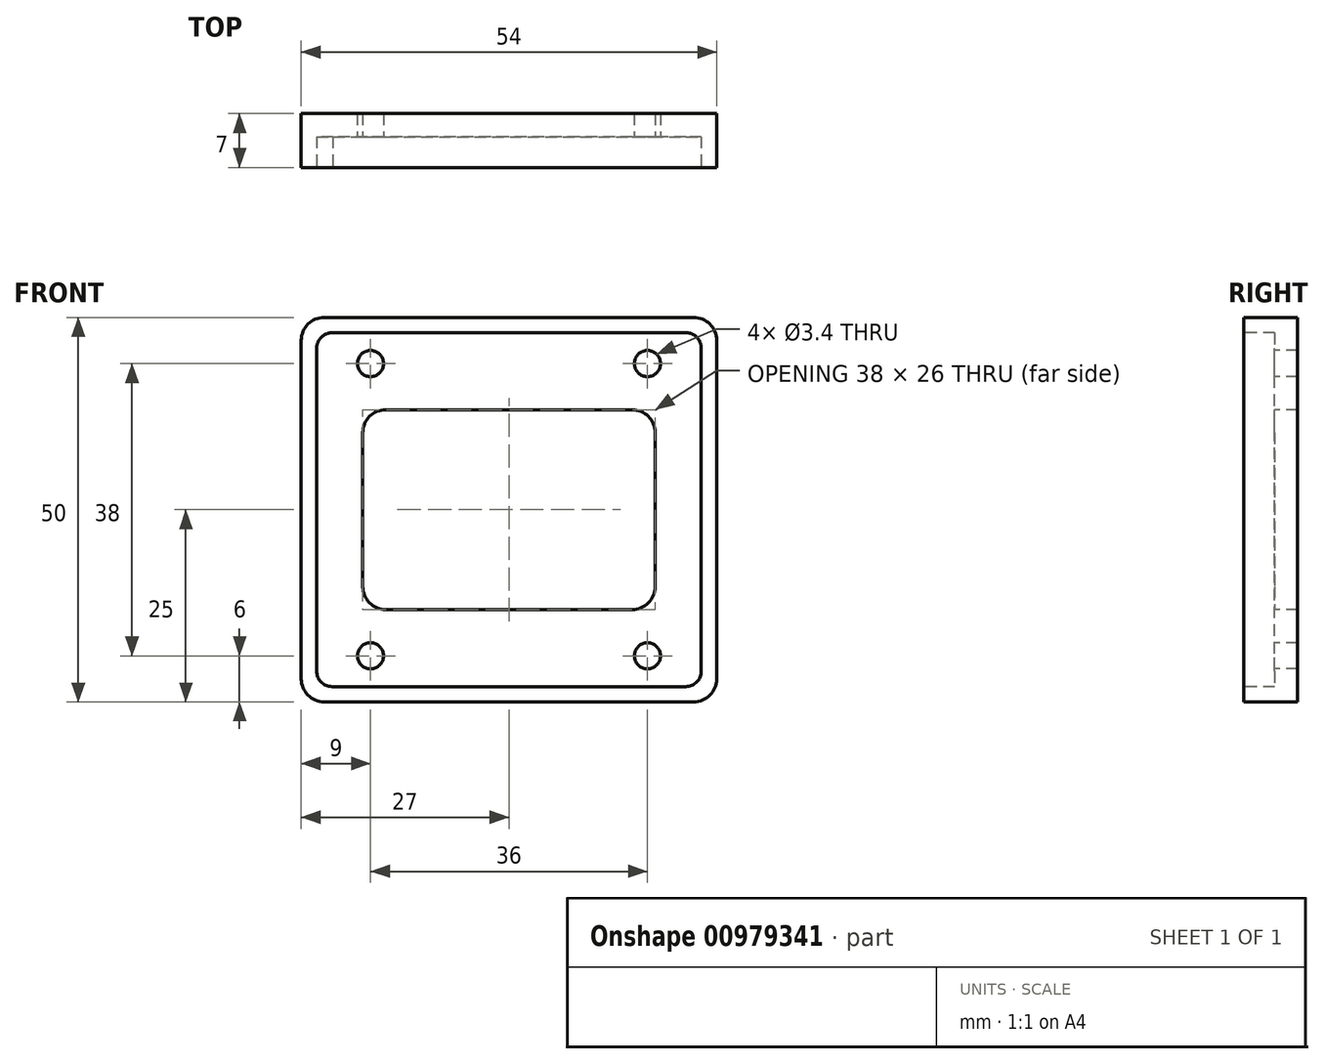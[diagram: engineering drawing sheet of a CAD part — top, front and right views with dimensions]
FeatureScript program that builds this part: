
annotation { "Feature Type Name" : "Feature", "Feature Type Description" : "" }
export const myFeature = defineFeature(function(context is Context, id is Id, definition is map)
    precondition{}
    {
        {
            var Q0;
            Q0=qCreatedBy(makeId("Front.planeOp"),FACE);
            var sketch = newSketch(context, id + "F0", { "sketchPlane" : qUnion([Q0])});
            skLineSegment(sketch, "E0.bottom", {"start": v(0, 0) * mm, "end": v(54, 0) * mm});
            skLineSegment(sketch, "E0.top", {"start": v(0, 50) * mm, "end": v(54, 50) * mm});
            skLineSegment(sketch, "E0.left", {"start": v(0, 0) * mm, "end": v(0, 50) * mm});
            skLineSegment(sketch, "E0.right", {"start": v(54, 0) * mm, "end": v(54, 50) * mm});
            skSolve(sketch);
        }
        {
            var Q0;
            Q0=makeQuery(id+"F0.imprint","IMPRINT",FACE,{"disambiguationData":[TD([[makeQuery(id+"F0.imprint","IMPRINT",EDGE,{"derivedFrom":sQuery(id+"F0.wireOp",EDGE,"E0.bottom")}),1.0]])]});
            extrude(context, id + "F1", {"entities" : qUnion([Q0]), "depth" : 7 * mm, "offsetDistance" : 25 * mm});
        }
        {
            var Q0;
            Q0=makeQuery(id+"F1.opExtrude","CAP_FACE",FACE,{"disambiguationData":[OSD([sQuery(id+"F0.wireOp",EDGE,"E0.bottom"),sQuery(id+"F0.wireOp",EDGE,"E0.top"),sQuery(id+"F0.wireOp",EDGE,"E0.left"),sQuery(id+"F0.wireOp",EDGE,"E0.right")])],"isStart":false});
            var sketch = newSketch(context, id + "F2", { "sketchPlane" : qUnion([Q0])});
            skPoint(sketch, "E1", {"position": v(27, 25) * mm});
            skPoint(sketch, "E1.positionSnap0", {"position": v(54, 25) * mm});
            skPoint(sketch, "E1.positionSnap1", {"position": v(27, 50) * mm});
            skPoint(sketch, "E2", {"position": v(9, 44) * mm});
            skPoint(sketch, "E3", {"position": v(45, 44) * mm});
            skPoint(sketch, "E4", {"position": v(45, 6) * mm});
            skPoint(sketch, "E5", {"position": v(9, 6) * mm});
            skSolve(sketch);
        }
        {
            var Q0;
            Q0=sQuery(id+"F2.wireOp",VERTEX,"E2");
            var Q1;
            Q1=sQuery(id+"F2.wireOp",VERTEX,"E3");
            var Q2;
            Q2=sQuery(id+"F2.wireOp",VERTEX,"E5");
            var Q3;
            Q3=sQuery(id+"F2.wireOp",VERTEX,"E4");
            var Q4;
            Q4=makeQuery(id+"F1.opExtrude","SWEPT_BODY",BODY,{"disambiguationData":[OSD([sQuery(id+"F0.wireOp",EDGE,"E0.bottom"),sQuery(id+"F0.wireOp",EDGE,"E0.top"),sQuery(id+"F0.wireOp",EDGE,"E0.left"),sQuery(id+"F0.wireOp",EDGE,"E0.right")])]});
            hole(context, id + "F3", {"style" : HoleStyle.SIMPLE, "endStyle" : HoleEndStyle.THROUGH, "standardTappedOrClearance" : lookupTablePath({ "fit" : "Normal", "standard" : "ISO", "size" : "M3", "type" : "Clearance" }), "standardBlindInLast" : lookupTablePath({ "fit" : "Normal", "standard" : "ISO", "engagement" : "75%", "pitch" : "0.5 mm", "size" : "M3", "type" : "Clearance & tapped" }), "holeDiameter" : 3.4 * mm, "majorDiameter" : 4 * mm, "isTappedThrough" : true, "tappedDepth" : 12.6 * mm, "tapClearance" : 3, "startFromSketch" : true, "locations" : qUnion([Q0, Q1, Q2, Q3]), "scope" : qUnion([Q4])});
        }
        {
            var Q0;
            Q0=makeQuery(id+"F2.imprint","IMPRINT",FACE,{"disambiguationData":[TD([[makeQuery(id+"F2.imprint","IMPRINT",EDGE,{"derivedFrom":makeQuery(id+"F1.opExtrude","CAP_EDGE",EDGE,{"disambiguationData":[OSD([sQuery(id+"F0.wireOp",EDGE,"E0.bottom")])],"isStart":false})}),1.0]])]});
            var sketch = newSketch(context, id + "F4", { "sketchPlane" : qUnion([Q0])});
            skPoint(sketch, "E6", {"position": v(11, 35) * mm});
            skPoint(sketch, "E7", {"position": v(43, 35) * mm});
            skPoint(sketch, "E8", {"position": v(43, 15) * mm});
            skPoint(sketch, "E9", {"position": v(11, 15) * mm});
            skArc(sketch, "E10", {"start": v(11, 38) * mm, "mid": v(8.88, 37.12) * mm, "end": v(8, 35) * mm});
            skArc(sketch, "E11", {"start": v(8, 15) * mm, "mid": v(8.88, 12.88) * mm, "end": v(11, 12) * mm});
            skArc(sketch, "E12", {"start": v(43, 12) * mm, "mid": v(45.12, 12.88) * mm, "end": v(46, 15) * mm});
            skArc(sketch, "E13", {"start": v(46, 35) * mm, "mid": v(45.12, 37.12) * mm, "end": v(43, 38) * mm});
            skLineSegment(sketch, "E14", {"start": v(8, 35) * mm, "end": v(8, 15) * mm});
            skLineSegment(sketch, "E15", {"start": v(11, 12) * mm, "end": v(43, 12) * mm});
            skLineSegment(sketch, "E16", {"start": v(46, 15) * mm, "end": v(46, 35) * mm});
            skLineSegment(sketch, "E17", {"start": v(43, 38) * mm, "end": v(11, 38) * mm});
            skSolve(sketch);
        }
        {
            var Q0;
            Q0 = qSketchRegion(id + "F4", true);
            extrude(context, id + "F5", {"entities" : qUnion([Q0]), "operationType" : NewBodyOperationType.REMOVE, "oppositeDirection" : true, "depth" : 25 * mm, "offsetDistance" : 25 * mm});
        }
        {
            var Q0;
            Q0=makeQuery(id+"F2.imprint","IMPRINT",FACE,{"disambiguationData":[TD([[makeQuery(id+"F2.imprint","IMPRINT",EDGE,{"derivedFrom":makeQuery(id+"F1.opExtrude","CAP_EDGE",EDGE,{"disambiguationData":[OSD([sQuery(id+"F0.wireOp",EDGE,"E0.bottom")])],"isStart":false})}),1.0]])]});
            var sketch = newSketch(context, id + "F6", { "sketchPlane" : qUnion([Q0])});
            skPoint(sketch, "E18", {"position": v(4, 46) * mm});
            skPoint(sketch, "E19", {"position": v(50, 46) * mm});
            skPoint(sketch, "E20", {"position": v(50, 4) * mm});
            skPoint(sketch, "E21", {"position": v(4, 4) * mm});
            skCircle(sketch, "E22", {"center": v(4, 46) * mm, "radius": 2 * mm});
            skCircle(sketch, "E23", {"center": v(50, 46) * mm, "radius": 2 * mm});
            skCircle(sketch, "E24", {"center": v(50, 4) * mm, "radius": 2 * mm});
            skCircle(sketch, "E25", {"center": v(4, 4) * mm, "radius": 2 * mm});
            skLineSegment(sketch, "E26", {"start": v(3.88, 48) * mm, "end": v(50, 48) * mm});
            skLineSegment(sketch, "E27", {"start": v(50, 48) * mm, "end": v(52, 46) * mm});
            skLineSegment(sketch, "E28", {"start": v(52, 46) * mm, "end": v(52, 4) * mm});
            skLineSegment(sketch, "E29", {"start": v(52, 4) * mm, "end": v(50, 2) * mm});
            skLineSegment(sketch, "E30", {"start": v(50, 2) * mm, "end": v(4, 2) * mm});
            skLineSegment(sketch, "E31", {"start": v(4, 2) * mm, "end": v(2, 4) * mm});
            skLineSegment(sketch, "E32", {"start": v(2, 4) * mm, "end": v(2, 46) * mm});
            skSolve(sketch);
        }
        {
            var Q0;
            Q0 = qSketchRegion(id + "F6", true);
            extrude(context, id + "F7", {"entities" : qUnion([Q0]), "operationType" : NewBodyOperationType.REMOVE, "oppositeDirection" : true, "depth" : 4 * mm, "offsetDistance" : 25 * mm});
        }
        {
            var Q0;
            Q0=makeQuery(id+"F1.opExtrude","SWEPT_EDGE",EDGE,{"disambiguationData":[OSD([sQuery(id+"F0.wireOp",EDGE,"E0.top"),sQuery(id+"F0.wireOp",EDGE,"E0.right")])]});
            var Q1;
            Q1=makeQuery(id+"F1.opExtrude","SWEPT_EDGE",EDGE,{"disambiguationData":[OSD([sQuery(id+"F0.wireOp",EDGE,"E0.bottom"),sQuery(id+"F0.wireOp",EDGE,"E0.right")])]});
            var Q2;
            Q2=makeQuery(id+"F1.opExtrude","SWEPT_EDGE",EDGE,{"disambiguationData":[OSD([sQuery(id+"F0.wireOp",EDGE,"E0.bottom"),sQuery(id+"F0.wireOp",EDGE,"E0.left")])]});
            var Q3;
            Q3=makeQuery(id+"F1.opExtrude","SWEPT_EDGE",EDGE,{"disambiguationData":[OSD([sQuery(id+"F0.wireOp",EDGE,"E0.top"),sQuery(id+"F0.wireOp",EDGE,"E0.left")])]});
            fillet(context, id + "F8", {"entities" : qUnion([Q0, Q1, Q2, Q3]), "radius" : 3 * mm, "tangentPropagation" : true, "allowEdgeOverflow" : false});
        }
    });
